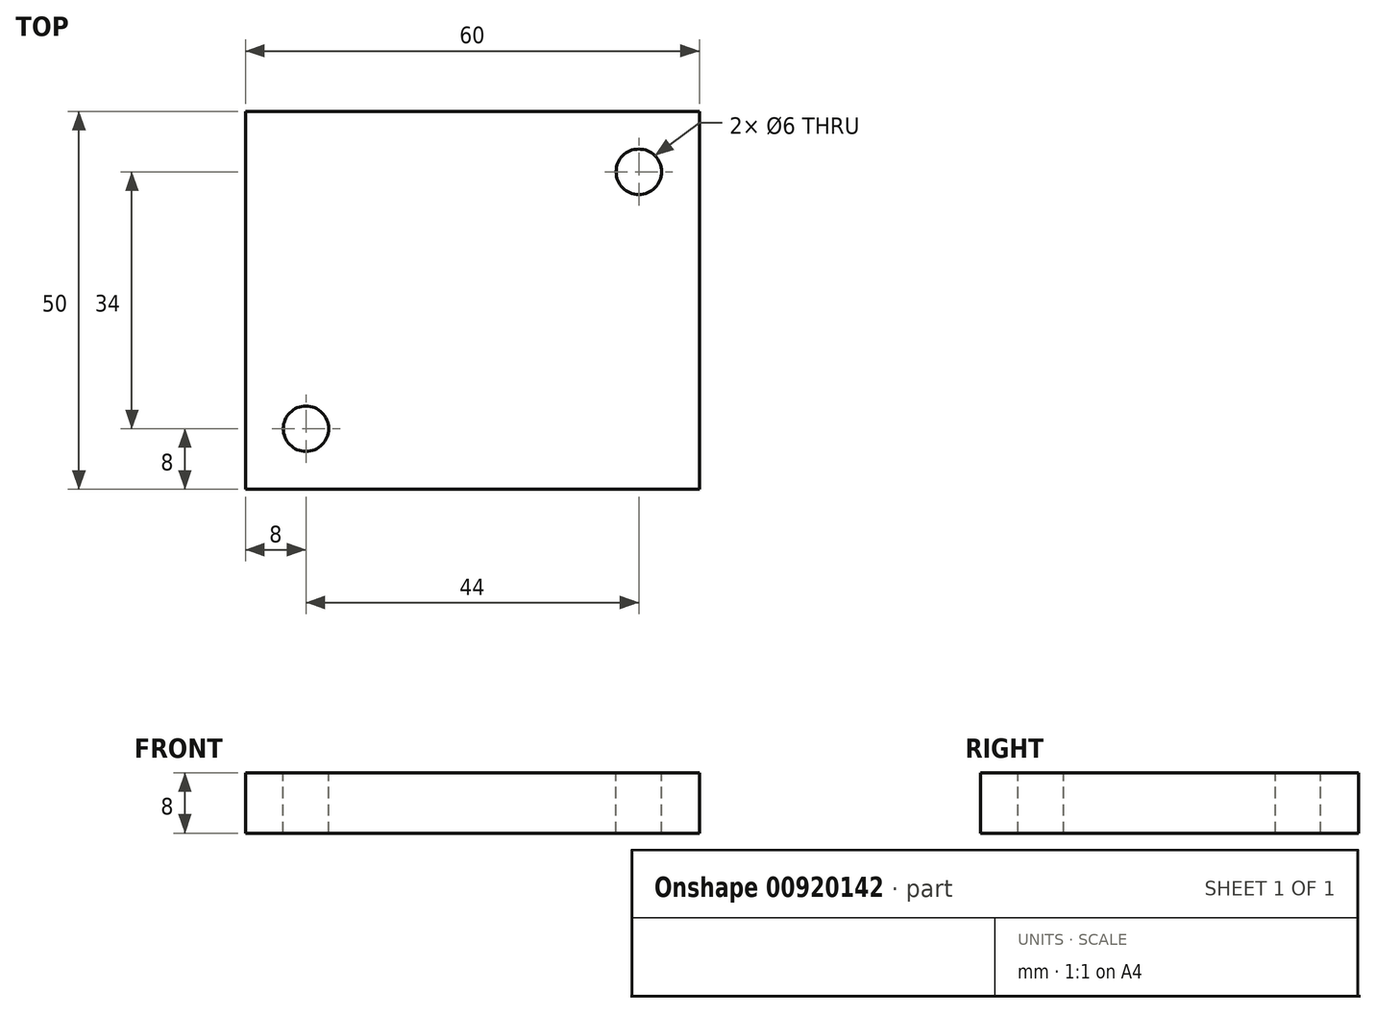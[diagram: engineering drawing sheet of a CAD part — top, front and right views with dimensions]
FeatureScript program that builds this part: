
annotation { "Feature Type Name" : "Feature", "Feature Type Description" : "" }
export const myFeature = defineFeature(function(context is Context, id is Id, definition is map)
    precondition{}
    {
        {
            var Q0;
            Q0=qCreatedBy(makeId("Top.planeOp"),FACE);
            var sketch = newSketch(context, id + "F0", { "sketchPlane" : qUnion([Q0])});
            skLineSegment(sketch, "E0.bottom", {"start": v(-30, -25) * mm, "end": v(30, -25) * mm});
            skLineSegment(sketch, "E0.top", {"start": v(-30, 25) * mm, "end": v(30, 25) * mm});
            skLineSegment(sketch, "E0.left", {"start": v(-30, -25) * mm, "end": v(-30, 25) * mm});
            skLineSegment(sketch, "E0.right", {"start": v(30, -25) * mm, "end": v(30, 25) * mm});
            skPoint(sketch, "E0.middle", {"position": v(0, 0) * mm});
            skSolve(sketch);
        }
        {
            var Q0;
            Q0=qSketchRegion(id+"F0",true);
            extrude(context, id + "F1", {"entities" : qUnion([Q0]), "depth" : 8 * mm, "offsetDistance" : 25 * mm});
        }
        {
            var Q0;
            Q0=makeQuery(id+"F1.opExtrude","CAP_FACE",FACE,{"disambiguationData":[OSD([sQuery(id+"F0.wireOp",EDGE,"E0.bottom"),sQuery(id+"F0.wireOp",EDGE,"E0.top"),sQuery(id+"F0.wireOp",EDGE,"E0.left"),sQuery(id+"F0.wireOp",EDGE,"E0.right")])],"isStart":false});
            var sketch = newSketch(context, id + "F2", { "sketchPlane" : qUnion([Q0])});
            skLineSegment(sketch, "E1.bottom", {"start": v(-22, -17) * mm, "end": v(22, -17) * mm});
            skLineSegment(sketch, "E1.top", {"start": v(-22, 17) * mm, "end": v(22, 17) * mm});
            skLineSegment(sketch, "E1.left", {"start": v(-22, -17) * mm, "end": v(-22, 17) * mm});
            skLineSegment(sketch, "E1.right", {"start": v(22, -17) * mm, "end": v(22, 17) * mm});
            skPoint(sketch, "E1.middle", {"position": v(0, 0) * mm});
            skPoint(sketch, "E2", {"position": v(-22, -17) * mm});
            skPoint(sketch, "E3", {"position": v(22, 17) * mm});
            skPoint(sketch, "E4", {"position": v(-22, 17) * mm});
            skPoint(sketch, "E5", {"position": v(22, -17) * mm});
            skSolve(sketch);
        }
        {
            var Q0;
            Q0=sQuery(id+"F2.wireOp",VERTEX,"E2");
            var Q1;
            Q1=sQuery(id+"F2.wireOp",VERTEX,"E3");
            var Q2;
            Q2=makeQuery(id+"F1.opExtrude","SWEPT_BODY",BODY,{"disambiguationData":[OSD([sQuery(id+"F0.wireOp",EDGE,"E0.bottom"),sQuery(id+"F0.wireOp",EDGE,"E0.top"),sQuery(id+"F0.wireOp",EDGE,"E0.left"),sQuery(id+"F0.wireOp",EDGE,"E0.right")])]});
            hole(context, id + "F3", {"style" : HoleStyle.SIMPLE, "endStyle" : HoleEndStyle.BLIND, "holeDiameter" : 6 * mm, "majorDiameter" : 5 * mm, "holeDepth" : 12 * mm, "isTappedThrough" : true, "tappedDepth" : 12 * mm, "tapClearance" : 3, "locations" : qUnion([Q0, Q1]), "scope" : qUnion([Q2])});
        }
    });
